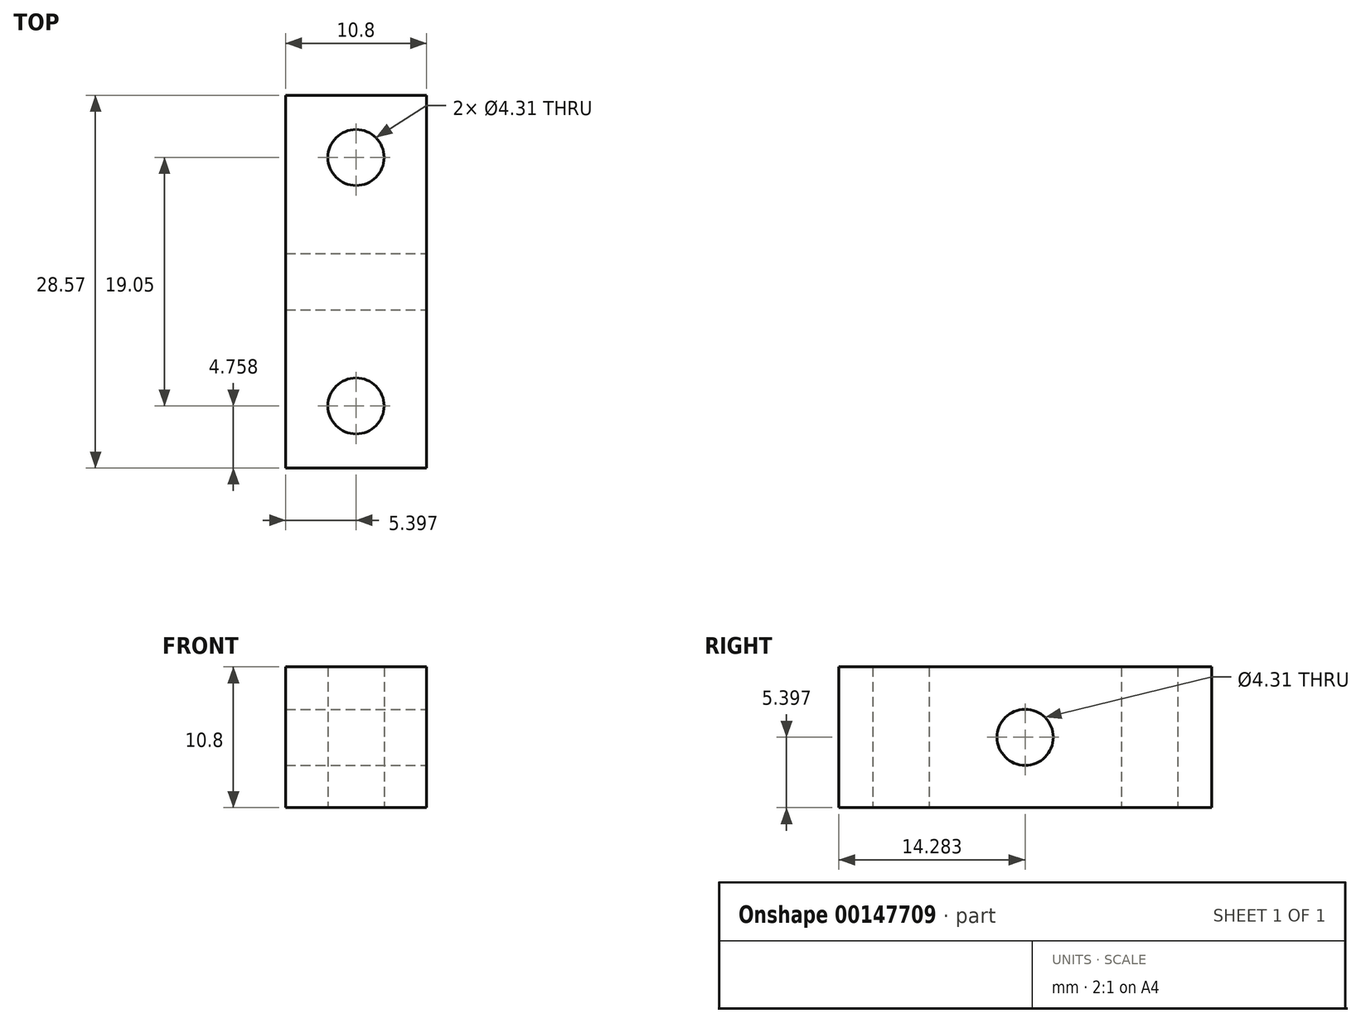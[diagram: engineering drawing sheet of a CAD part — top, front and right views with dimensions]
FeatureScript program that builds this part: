
annotation { "Feature Type Name" : "Feature", "Feature Type Description" : "" }
export const myFeature = defineFeature(function(context is Context, id is Id, definition is map)
    precondition{}
    {
        {
            var Q0;
            Q0=qCreatedBy(makeId("Top.planeOp"),FACE);
            var sketch = newSketch(context, id + "F0", { "sketchPlane" : qUnion([Q0])});
            skLineSegment(sketch, "E0.bottom", {"start": v(0, 0) * mm, "end": v(10.8, 0) * mm});
            skLineSegment(sketch, "E0.top", {"start": v(0, -28.57) * mm, "end": v(10.8, -28.57) * mm});
            skLineSegment(sketch, "E0.left", {"start": v(0, 0) * mm, "end": v(0, -28.58) * mm});
            skLineSegment(sketch, "E0.right", {"start": v(10.8, 0) * mm, "end": v(10.8, -28.57) * mm});
            skLineSegment(sketch, "E1", {"start": v(5.4, 0) * mm, "end": v(5.4, -4.76) * mm, "construction": true});
            skLineSegment(sketch, "E2", {"start": v(5.4, -4.76) * mm, "end": v(5.4, -23.81) * mm, "construction": true});
            skCircle(sketch, "E3", {"center": v(5.4, -4.76) * mm, "radius": 2.15 * mm});
            skCircle(sketch, "E4", {"center": v(5.4, -23.81) * mm, "radius": 2.15 * mm});
            skLineSegment(sketch, "E5", {"start": v(5.4, -23.81) * mm, "end": v(5.4, -28.57) * mm, "construction": true});
            skSolve(sketch);
        }
        {
            var Q0;
            Q0=qSketchRegion(id+"F0",true);
            extrude(context, id + "F1", {"entities" : qUnion([Q0]), "depth" : 10.8 * mm});
        }
        {
            var Q0;
            Q0=makeQuery(id+"F1.opExtrude","SWEPT_FACE",FACE,{"disambiguationData":[OSD([sQuery(id+"F0.wireOp",EDGE,"E0.right")])]});
            var sketch = newSketch(context, id + "F2", { "sketchPlane" : qUnion([Q0])});
            skCircle(sketch, "E6", {"center": v(-14.29, 5.4) * mm, "radius": 2.15 * mm});
            skLineSegment(sketch, "E7", {"start": v(-14.29, 5.4) * mm, "end": v(-14.29, 0) * mm, "construction": true});
            skLineSegment(sketch, "E8", {"start": v(-14.29, 5.4) * mm, "end": v(-14.29, 10.8) * mm, "construction": true});
            skSolve(sketch);
        }
        {
            var Q0;
            Q0=qSketchRegion(id+"F2",true);
            var Q1;
            Q1=makeQuery(id+"F1.opExtrude","SWEPT_FACE",FACE,{"disambiguationData":[OSD([sQuery(id+"F0.wireOp",EDGE,"E0.left")])]});
            extrude(context, id + "F3", {"entities" : qUnion([Q0]), "operationType" : NewBodyOperationType.REMOVE, "endBound" : BoundingType.UP_TO_SURFACE, "oppositeDirection" : true, "endBoundEntityFace" : qUnion([Q1]), "depth" : 25.4 * mm});
        }
    });
